FCSTD DOCUMENT  (FreeCAD 0.16R)
Label: cap9
License: All rights reserved
LicenseURL: http://en.wikipedia.org/wiki/All_rights_reserved
objects: Sketcher::SketchObject×5, PartDesign::Pocket×3, PartDesign::Pad×1, PartDesign::Chamfer×1, PartDesign::Fillet×1, Mesh::Feature×1
note: 15 computed .brp shape members not serialized (recipe doc carries the construction recipe); baked Part::Feature solids carry a one-line shape summary decoded from their .brp

FEATURE [Sketcher::SketchObject] Sketch
FEATURE [Sketcher::SketchObject] Sketch003
  Placement = pos=(0,0,-6) rot=(1,0,0;3.14159rad)
  sketch-geometry (7):
    g0: LineSegment StartX=-39.7363 StartY=0 StartZ=0 EndX=0 EndY=0 EndZ=0
    g1: LineSegment StartX=0 StartY=0 StartZ=0 EndX=2.92372 EndY=9.56305 EndZ=0
    g2: LineSegment StartX=2.92372 StartY=9.56305 StartZ=0 EndX=-33.4159 EndY=20.6732 EndZ=0
    g3: LineSegment StartX=-33.4159 StartY=20.6732 StartZ=0 EndX=-39.7363 EndY=0 EndZ=0
    g4: LineSegment [constr] StartX=-6.16153 StartY=44.8323 StartZ=0 EndX=-26.2639 EndY=-20.9195 EndZ=0
    g5: LineSegment StartX=-39.7363 StartY=0 StartZ=0 EndX=0 EndY=0 EndZ=0
    g6: LineSegment StartX=-39.7363 StartY=0 StartZ=0 EndX=0 EndY=0 EndZ=0
  constraints (20):
    c: Horizontal(g0)
    c: Coincident(g0,g1)
    c: Coincident(g1,g2)
    c: Coincident(g2,g3)
    c: Coincident(g3,g0)
    c: Parallel(g1,g3)
    c: Perpendicular(g3,g2)
    c: Distance(g2) = 38
    c: Perpendicular(g4,g2)
    c: Symmetric(g1,g2,g4)
    c: Distance(g1) = 10
    c: Angle(g4) = -1.8675
    c: DistanceX(g0) = 0
    c: Distance(g4) = 68.7561
    c: DistanceY(g4) = 44.8323
    c: Coincident(g5,g0)
    c: PointOnObject(g5,g-1)
    c: Coincident(g6,g0)
    c: Coincident(g6,g5)
    c: Coincident(g5,g0)
FEATURE [PartDesign::Pad] Pad
  Length = 16
  Length2 = 100
  Placement = pos=(0,0,-6) rot=(1,0,0;3.14159rad)
  Sketch = -> Sketch003
  Type = 0
FEATURE [Sketcher::SketchObject] Sketch004
  ExternalGeometry = -> [Pad]
  Placement = pos=(2.92372,-9.56305,-6) rot=(-0.105093,0.703191,-0.703191;2.93218rad)
  Support = -> Pad [Face2]
  sketch-geometry (1):
    g0: Circle CenterX=19 CenterY=0 CenterZ=0 NormalX=0 NormalY=0 NormalZ=1 Radius=12.7
  constraints (2):
    c: Radius(g0) = 12.7
    c: Symmetric(g-3,g-1,g0)
FEATURE [PartDesign::Pocket] Pocket
  Length = 5
  Placement = pos=(0,0,-6) rot=(1,0,0;3.14159rad)
  Sketch = -> Sketch004
  Type = 1
FEATURE [Sketcher::SketchObject] Sketch005
  ExternalGeometry = -> [Pocket]
  Placement = pos=(0,0,-6) rot=(0,0,1;0rad)
  Support = -> Pocket [Face6]
  sketch-geometry (3):
    g0: Circle CenterX=-1.69395 CenterY=-5.74635 CenterZ=0 NormalX=0 NormalY=0 NormalZ=1 Radius=1.8
    g1: Circle CenterX=-34.6456 CenterY=-5.36377 CenterZ=0 NormalX=0 NormalY=0 NormalZ=1 Radius=1.8
    g2: Circle CenterX=-31.7219 CenterY=-14.9268 CenterZ=0 NormalX=0 NormalY=0 NormalZ=1 Radius=1.8
  constraints (9):
    c: Radius(g2) = 1.8
    c: Equal(g2,g1)
    c: Equal(g2,g0)
    c: Distance(g0,g-6) = 3
    c: Distance(g2,g-3) = 3
    c: Distance(g1,g-3) = 3
    c: Distance(g2,g-7) = 5
    c: Distance(g2,g1) = 10
    c: Distance(g0,g-8) = 5
FEATURE [PartDesign::Pocket] Pocket001
  Length = 5
  Placement = pos=(0,0,-6) rot=(1,0,0;3.14159rad)
  Sketch = -> Sketch005
  Type = 1
FEATURE [Sketcher::SketchObject] Sketch006
  Placement = pos=(0,0,-6) rot=(0,0,1;0rad)
  Support = -> Pocket001 [Face4]
  sketch-geometry (1):
    g0: Circle CenterX=0 CenterY=0 CenterZ=0 NormalX=0 NormalY=0 NormalZ=1 Radius=50
  constraints (2):
    c: Coincident(g0,g-1)
    c: Radius(g0) = 50
FEATURE [PartDesign::Pocket] Pocket002
  Length = 1
  Placement = pos=(0,0,-6) rot=(1,0,0;3.14159rad)
  Sketch = -> Sketch006
  Type = 0
FEATURE [PartDesign::Chamfer] Chamfer
  Base = -> Pocket002 [Edge12,Edge3,Edge13,Edge14]
  Placement = pos=(0,0,-6) rot=(1,0,0;3.14159rad)
  Size = 1
FEATURE [PartDesign::Fillet] Fillet
  Base = -> Chamfer [Edge4,Edge1,Edge5,Edge17]
  Placement = pos=(0,0,-6) rot=(1,0,0;3.14159rad)
  Radius = 1
FEATURE [Mesh::Feature] Mesh  label="Fillet (Meshed)"
